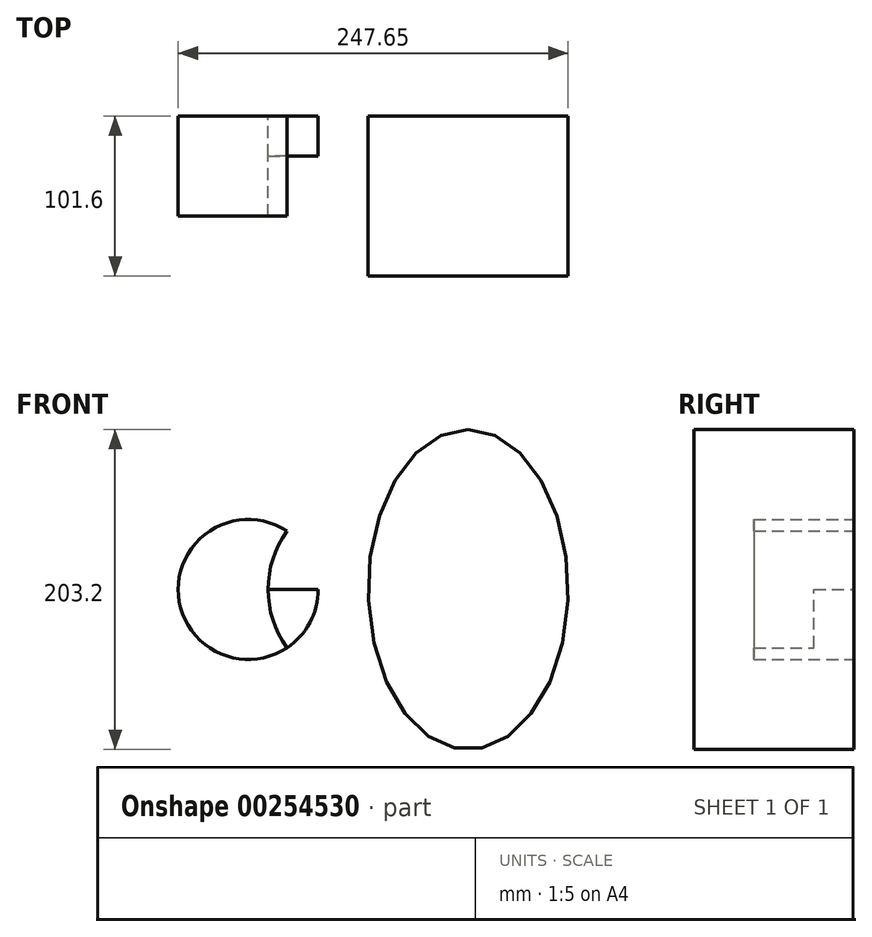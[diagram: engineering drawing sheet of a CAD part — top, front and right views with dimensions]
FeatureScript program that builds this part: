
annotation { "Feature Type Name" : "Feature", "Feature Type Description" : "" }
export const myFeature = defineFeature(function(context is Context, id is Id, definition is map)
    precondition{}
    {
        {
            var Q0;
            Q0=qCreatedBy(makeId("Front.planeOp"),FACE);
            var sketch = newSketch(context, id + "F0", { "sketchPlane" : qUnion([Q0])});
            skLineSegment(sketch, "E0", {"start": v(0, 0) * mm, "end": v(-76.2, 0) * mm});
            skCircle(sketch, "E1", {"center": v(-76.2, 0) * mm, "radius": 44.45 * mm});
            skLineSegment(sketch, "E2", {"start": v(0, 0) * mm, "end": v(-63.5, 0) * mm});
            skCircle(sketch, "E3", {"center": v(0, 0) * mm, "radius": 63.5 * mm});
            skLineSegment(sketch, "E4", {"start": v(63.5, 0) * mm, "end": v(63.5, 101.6) * mm});
            skEllipse(sketch, "E5", {"center": v(63.5, 0) * mm, "majorRadius": 101.6 * mm, "minorRadius": 63.5 * mm, "majorAxis": v(0, 1)});
            skSolve(sketch);
        }
        {
            var Q0;
            {var subQ0=sQuery(id+"F0.wireOp",EDGE,"E3");var subQ1=sQuery(id+"F0.wireOp",EDGE,"E1");var subQ2=makeQuery(id+"F0.imprint","INTERSECT",VERTEX,{"disambiguationData":[OD(0.0)],"derivedFrom":[subQ1,subQ0]});Q0=makeQuery(id+"F0.imprint","IMPRINT",FACE,{"disambiguationData":[TD([[makeQuery(id+"F0.imprint","IMPRINT",EDGE,{"disambiguationData":[TD([[subQ2,-1.0]])],"derivedFrom":subQ1}),1.0]])]});}
            extrude(context, id + "F1", {"entities" : qUnion([Q0]), "depth" : 25.4 * mm});
        }
        {
            var Q0;
            {var subQ0=sQuery(id+"F0.wireOp",EDGE,"E3");var subQ1=sQuery(id+"F0.wireOp",EDGE,"E1");var subQ2=makeQuery(id+"F0.imprint","INTERSECT",VERTEX,{"disambiguationData":[OD(0.0)],"derivedFrom":[subQ1,subQ0]});Q0=makeQuery(id+"F0.imprint","IMPRINT",FACE,{"disambiguationData":[TD([[makeQuery(id+"F0.imprint","IMPRINT",EDGE,{"disambiguationData":[TD([[subQ2,1.0]])],"derivedFrom":subQ1}),1.0]])]});}
            var Q1;
            {var subQ0=sQuery(id+"F0.wireOp",EDGE,"E3");var subQ1=sQuery(id+"F0.wireOp",EDGE,"E1");var subQ2=makeQuery(id+"F0.imprint","INTERSECT",VERTEX,{"disambiguationData":[OD(1.0)],"derivedFrom":[subQ1,subQ0]});Q1=makeQuery(id+"F0.imprint","IMPRINT",FACE,{"disambiguationData":[TD([[makeQuery(id+"F0.imprint","IMPRINT",EDGE,{"disambiguationData":[TD([[subQ2,-1.0]])],"derivedFrom":subQ1}),1.0]])]});}
            var Q2;
            {var subQ0=sQuery(id+"F0.wireOp",EDGE,"E3");var subQ1=sQuery(id+"F0.wireOp",EDGE,"E1");var subQ2=makeQuery(id+"F0.imprint","INTERSECT",VERTEX,{"disambiguationData":[OD(1.0)],"derivedFrom":[subQ1,subQ0]});Q2=makeQuery(id+"F0.imprint","IMPRINT",FACE,{"disambiguationData":[TD([[makeQuery(id+"F0.imprint","IMPRINT",EDGE,{"disambiguationData":[TD([[subQ2,-1.0]])],"derivedFrom":subQ1}),-1.0]])]});}
            var Q3;
            {var subQ0=sQuery(id+"F0.wireOp",EDGE,"E3");var subQ1=sQuery(id+"F0.wireOp",EDGE,"E1");var subQ2=makeQuery(id+"F0.imprint","INTERSECT",VERTEX,{"disambiguationData":[OD(0.0)],"derivedFrom":[subQ1,subQ0]});Q3=makeQuery(id+"F0.imprint","IMPRINT",FACE,{"disambiguationData":[TD([[makeQuery(id+"F0.imprint","IMPRINT",EDGE,{"disambiguationData":[TD([[subQ2,1.0]])],"derivedFrom":subQ1}),-1.0]])]});}
            extrude(context, id + "F2", {"entities" : qUnion([Q0, Q1, Q2, Q3]), "operationType" : NewBodyOperationType.ADD, "depth" : 63.5 * mm});
        }
        {
            var Q0;
            {var subQ0=sQuery(id+"F0.wireOp",EDGE,"E4");Q0=makeQuery(id+"F0.imprint","IMPRINT",FACE,{"disambiguationData":[TD([[makeQuery(id+"F0.imprint","IMPRINT",EDGE,{"derivedFrom":subQ0}),-1.0]])]});}
            var Q1;
            {var subQ0=sQuery(id+"F0.wireOp",EDGE,"E3");var subQ1=makeQuery(id+"F0.imprint","INTERSECT",VERTEX,{"derivedFrom":[subQ0,sQuery(id+"F0.wireOp",EDGE,"E4")]});Q1=makeQuery(id+"F0.imprint","IMPRINT",FACE,{"disambiguationData":[TD([[makeQuery(id+"F0.imprint","IMPRINT",EDGE,{"disambiguationData":[TD([[subQ1,-1.0]])],"derivedFrom":subQ0}),1.0]])]});}
            var Q2;
            {var subQ0=sQuery(id+"F0.wireOp",EDGE,"E4");Q2=makeQuery(id+"F0.imprint","IMPRINT",FACE,{"disambiguationData":[TD([[makeQuery(id+"F0.imprint","IMPRINT",EDGE,{"derivedFrom":subQ0}),1.0]])]});}
            extrude(context, id + "F3", {"entities" : qUnion([Q0, Q1, Q2]), "operationType" : NewBodyOperationType.ADD, "depth" : 101.6 * mm});
        }
    });
